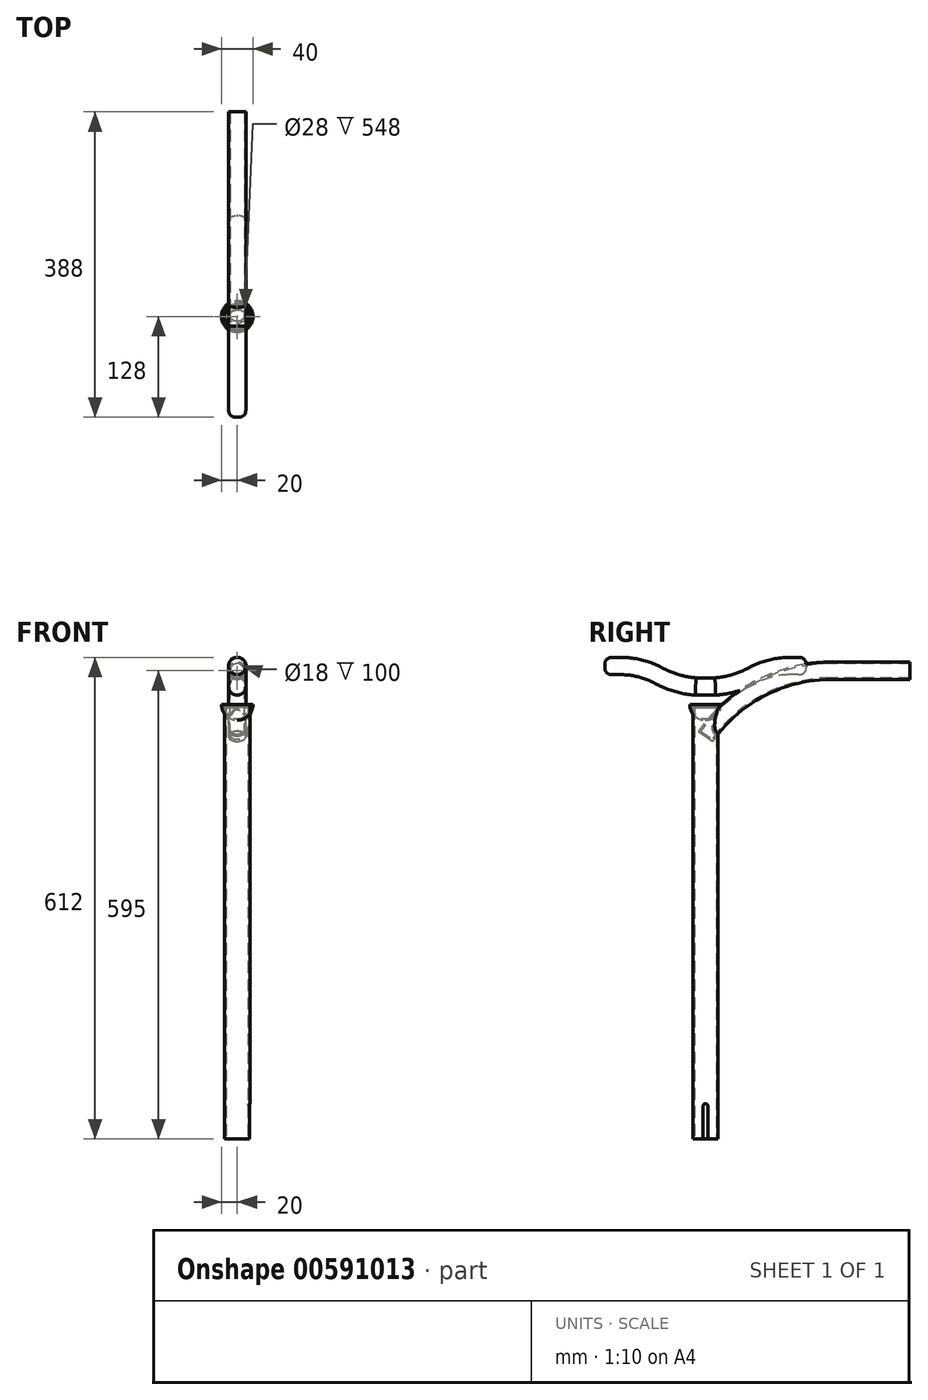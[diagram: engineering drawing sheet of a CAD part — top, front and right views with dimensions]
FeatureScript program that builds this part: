
annotation { "Feature Type Name" : "Feature", "Feature Type Description" : "" }
export const myFeature = defineFeature(function(context is Context, id is Id, definition is map)
    precondition{}
    {
        {
            var Q0;
            Q0=qCreatedBy(makeId("Top.planeOp"),FACE);
            var sketch = newSketch(context, id + "F0", { "sketchPlane" : qUnion([Q0])});
            skCircle(sketch, "E0", {"center": v(0, 0) * mm, "radius": 16 * mm});
            skSolve(sketch);
        }
        {
            var Q0;
            Q0 = qSketchRegion(id + "F0", true);
            extrude(context, id + "F1", {"entities" : qUnion([Q0]), "depth" : 550 * mm, "offsetDistance" : 25 * mm});
        }
        {
            var Q0;
            Q0=makeQuery(id+"F1.opExtrude","CAP_FACE",FACE,{"disambiguationData":[OSD([sQuery(id+"F0.wireOp",EDGE,"E0")])],"isStart":true});
            shell(context, id + "F2", {"entities" : qUnion([Q0]), "thickness" : 2 * mm});
        }
        {
            var Q0;
            Q0=qCreatedBy(makeId("Right.planeOp"),FACE);
            var sketch = newSketch(context, id + "F3", { "sketchPlane" : qUnion([Q0])});
            skLineSegment(sketch, "E1.bottom", {"start": v(-3, 0) * mm, "end": v(3, 0) * mm});
            skLineSegment(sketch, "E1.top", {"start": v(0, 45) * mm, "end": v(0, 45) * mm});
            skLineSegment(sketch, "E1.left", {"start": v(-3, 0) * mm, "end": v(-3, 42) * mm});
            skLineSegment(sketch, "E1.right", {"start": v(3, 0) * mm, "end": v(3, 42) * mm});
            skPoint(sketch, "E2.visualSharp", {"position": v(-3, 45) * mm});
            skArc(sketch, "E2.filletArc", {"start": v(0, 45) * mm, "mid": v(-2.12, 44.12) * mm, "end": v(-3, 42) * mm});
            skPoint(sketch, "E3.visualSharp", {"position": v(3, 45) * mm});
            skArc(sketch, "E3.filletArc", {"start": v(3, 42) * mm, "mid": v(2.12, 44.12) * mm, "end": v(0, 45) * mm});
            skSolve(sketch);
        }
        {
            var Q0;
            Q0 = qSketchRegion(id + "F3", true);
            extrude(context, id + "F4", {"entities" : qUnion([Q0]), "operationType" : NewBodyOperationType.REMOVE, "endBound" : BoundingType.THROUGH_ALL, "depth" : 25 * mm, "offsetDistance" : 25 * mm});
        }
        {
            var Q0;
            Q0=qCreatedBy(makeId("Right.planeOp"),FACE);
            var sketch = newSketch(context, id + "F5", { "sketchPlane" : qUnion([Q0])});
            skArc(sketch, "E4", {"start": v(160, 595) * mm, "mid": v(69.75, 572.86) * mm, "end": v(0, 511.47) * mm});
            skLineSegment(sketch, "E5", {"start": v(160, 595) * mm, "end": v(260, 595) * mm});
            skSolve(sketch);
        }
        {
            var Q0;
            Q0=sQuery(id+"F5.wireOp",VERTEX,"E5.end");
            var Q1;
            Q1=qCreatedBy(makeId("Front.planeOp"),FACE);
            cPlane(context, id + "F6", {"entities" : qUnion([Q0, Q1]), "cplaneType" : CPlaneType.PLANE_POINT, "offset" : 25 * mm, "width" : 150 * mm, "height" : 150 * mm});
        }
        {
            var Q0;
            Q0=qCreatedBy(id+"F6.planeOp",FACE);
            var sketch = newSketch(context, id + "F7", { "sketchPlane" : qUnion([Q0])});
            skCircle(sketch, "E6", {"center": v(0, 595) * mm, "radius": 11 * mm});
            skSolve(sketch);
        }
        {
            var Q0;
            Q0 = qSketchRegion(id + "F7", true);
            var Q1;
            Q1 = qConstructionFilter(qBodyType(qCreatedBy(id + "F5" ,EDGE), BodyType.WIRE), ConstructionObject.NO);
            sweep(context, id + "F8", {"operationType" : NewBodyOperationType.ADD, "profiles" : qUnion([Q0]), "path" : qUnion([Q1])});
        }
        {
            var Q0;
            Q0=makeQuery(id+"F8.opSweep","CAP_FACE",FACE,{"disambiguationData":[OSD([sQuery(id+"F5.wireOp",VERTEX,"E5.end"),sQuery(id+"F7.wireOp",EDGE,"E6")])],"isStart":true});
            shell(context, id + "F9", {"entities" : qUnion([Q0]), "thickness" : 2 * mm});
        }
        {
            var Q0;
            Q0=qCreatedBy(makeId("Right.planeOp"),FACE);
            var sketch = newSketch(context, id + "F10", { "sketchPlane" : qUnion([Q0])});
            skLineSegment(sketch, "E7", {"start": v(-128, 601) * mm, "end": v(-108, 601) * mm});
            skArc(sketch, "E8", {"start": v(-58.75, 588.44) * mm, "mid": v(-82.59, 597.81) * mm, "end": v(-108, 601) * mm});
            skArc(sketch, "E9", {"start": v(-58.75, 588.44) * mm, "mid": v(-36.36, 579.2) * mm, "end": v(-12.5, 575) * mm});
            skLineSegment(sketch, "E10", {"start": v(-12.5, 575) * mm, "end": v(0, 575) * mm});
            skLineSegment(sketch, "E11", {"start": v(0, 495.83) * mm, "end": v(0, 711.1) * mm, "construction": true});
            skLineSegment(sketch, "E12.MirrorCS", {"start": v(12.5, 575) * mm, "end": v(0, 575) * mm});
            skArc(sketch, "E13.MirrorCS", {"start": v(58.75, 588.44) * mm, "mid": v(36.36, 579.2) * mm, "end": v(12.5, 575) * mm});
            skArc(sketch, "E14.MirrorCS", {"start": v(58.75, 588.44) * mm, "mid": v(82.59, 597.81) * mm, "end": v(108, 601) * mm});
            skLineSegment(sketch, "E15.MirrorCS", {"start": v(128, 601) * mm, "end": v(108, 601) * mm});
            skSolve(sketch);
        }
        {
            var Q0;
            Q0=sQuery(id+"F10.wireOp",VERTEX,"E15.MirrorCS.start");
            var Q1;
            Q1=qCreatedBy(id+"F6.planeOp",FACE);
            cPlane(context, id + "F11", {"entities" : qUnion([Q0, Q1]), "cplaneType" : CPlaneType.PLANE_POINT, "offset" : 25 * mm, "width" : 150 * mm, "height" : 150 * mm});
        }
        {
            var Q0;
            Q0=qCreatedBy(id+"F11.planeOp",FACE);
            var sketch = newSketch(context, id + "F12", { "sketchPlane" : qUnion([Q0])});
            skCircle(sketch, "E16", {"center": v(0, 601) * mm, "radius": 11 * mm});
            skSolve(sketch);
        }
        {
            var Q0;
            Q0 = qSketchRegion(id + "F12", true);
            var Q1;
            Q1 = qConstructionFilter(qBodyType(qCreatedBy(id + "F10" ,EDGE), BodyType.WIRE), ConstructionObject.NO);
            sweep(context, id + "F13", {"profiles" : qUnion([Q0]), "path" : qUnion([Q1])});
        }
        {
            var Q0;
            Q0=makeQuery(id+"F13.opSweep","CAP_EDGE",EDGE,{"disambiguationData":[OSD([sQuery(id+"F10.wireOp",VERTEX,"E7.start"),sQuery(id+"F12.wireOp",EDGE,"E16")])],"isStart":false});
            var Q1;
            {var subQ0=sQuery(id+"F12.wireOp",EDGE,"E16");var subQ1=sQuery(id+"F10.wireOp",VERTEX,"E15.MirrorCS.start");Q1=makeQuery(id+"F13.boolean.opBoolean","SPLIT",EDGE,{"disambiguationData":[TD([makeQuery(id+"F8.opSweep","SWEPT_FACE",FACE,{"disambiguationData":[OSD([sQuery(id+"F5.wireOp",EDGE,"E4"),sQuery(id+"F7.wireOp",EDGE,"E6")])]})])],"derivedFrom":makeQuery(id+"F13.opSweep","CAP_EDGE",EDGE,{"disambiguationData":[OSD([subQ1,subQ0])],"isStart":true})});}
            fillet(context, id + "F14", {"entities" : qUnion([Q0, Q1]), "radius" : 10 * mm, "tangentPropagation" : true, "rho" : 0.5, "crossSection" : FilletCrossSection.CONIC, "allowEdgeOverflow" : false});
        }
        {
            var Q0;
            Q0=qCreatedBy(makeId("Right.planeOp"),FACE);
            var sketch = newSketch(context, id + "F15", { "sketchPlane" : qUnion([Q0])});
            skArc(sketch, "E17", {"start": v(-20, 552) * mm, "mid": v(-14.14, 537.86) * mm, "end": v(0, 532) * mm});
            skLineSegment(sketch, "E18", {"start": v(0, 532) * mm, "end": v(0, 552) * mm});
            skLineSegment(sketch, "E19", {"start": v(0, 552) * mm, "end": v(-20, 552) * mm});
            skSolve(sketch);
        }
        {
            var Q0;
            Q0 = qSketchRegion(id + "F15", true);
            var Q1;
            Q1=makeQuery(id+"F1.opExtrude","CAP_EDGE",EDGE,{"disambiguationData":[OSD([sQuery(id+"F0.wireOp",EDGE,"E0")])],"isStart":false});
            revolve(context, id + "F16", {"surfaceOperationType" : NewSurfaceOperationType.NEW, "entities" : qUnion([Q0]), "axis" : qUnion([Q1]), "revolveType" : RevolveType.FULL});
        }
        {
            var Q0;
            Q0=makeQuery(id+"F16.opRevolve","SWEPT_FACE",FACE,{"disambiguationData":[OSD([sQuery(id+"F15.wireOp",EDGE,"E19")])]});
            shell(context, id + "F17", {"entities" : qUnion([Q0]), "thickness" : 2 * mm});
        }
    });
